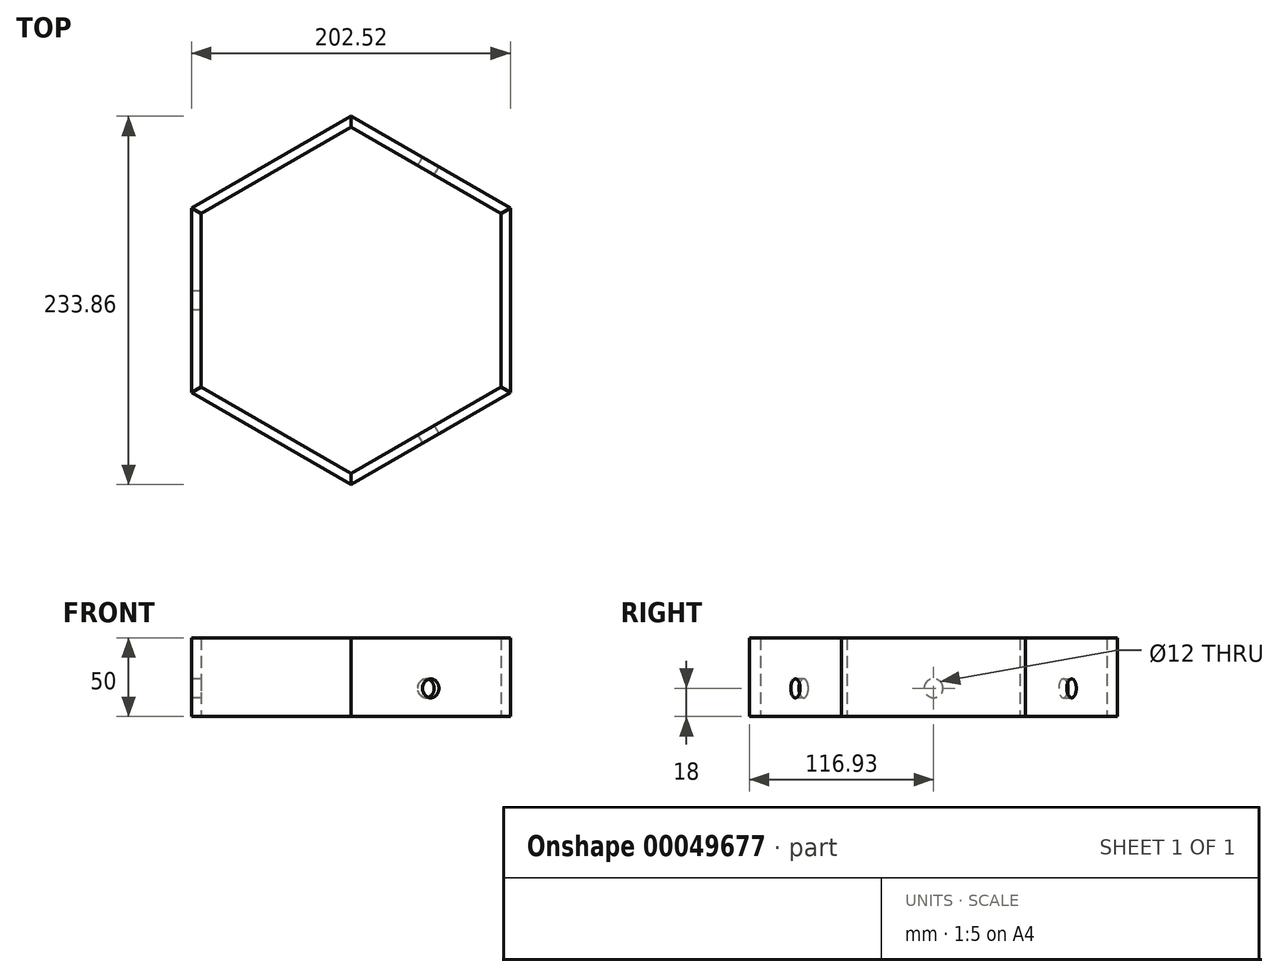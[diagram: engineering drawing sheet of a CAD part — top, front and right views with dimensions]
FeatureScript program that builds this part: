
annotation { "Feature Type Name" : "Feature", "Feature Type Description" : "" }
export const myFeature = defineFeature(function(context is Context, id is Id, definition is map)
    precondition{}
    {
        {
            var Q0;
            Q0=qCreatedBy(makeId("Top.planeOp"),FACE);
            var sketch = newSketch(context, id + "F0", { "sketchPlane" : qUnion([Q0])});
            skCircle(sketch, "E0.cCircle", {"center": v(0, 0) * mm, "radius": 101.26 * mm, "construction": true});
            skLineSegment(sketch, "E0.0", {"start": v(101.26, -58.46) * mm, "end": v(0, -116.93) * mm});
            skLineSegment(sketch, "E0.1", {"start": v(0, -116.93) * mm, "end": v(-101.26, -58.46) * mm});
            skLineSegment(sketch, "E0.2", {"start": v(-101.26, -58.46) * mm, "end": v(-101.26, 58.46) * mm});
            skLineSegment(sketch, "E0.3", {"start": v(-101.26, 58.46) * mm, "end": v(0, 116.93) * mm});
            skLineSegment(sketch, "E0.4", {"start": v(0, 116.93) * mm, "end": v(101.26, 58.46) * mm});
            skLineSegment(sketch, "E0.5", {"start": v(101.26, 58.46) * mm, "end": v(101.26, -58.46) * mm});
            skPoint(sketch, "E0.0.midPoint", {"position": v(50.63, -87.7) * mm});
            skLineSegment(sketch, "E1", {"start": v(0, 116.93) * mm, "end": v(0, -116.93) * mm, "construction": true});
            skLineSegment(sketch, "E2.0", {"start": v(-95.26, -55) * mm, "end": v(-95.26, 55) * mm});
            skLineSegment(sketch, "E2.1", {"start": v(0, 110) * mm, "end": v(95.26, 55) * mm});
            skLineSegment(sketch, "E2.2", {"start": v(95.26, 55) * mm, "end": v(95.26, -55) * mm});
            skLineSegment(sketch, "E2.3", {"start": v(-95.26, 55) * mm, "end": v(0, 110) * mm});
            skLineSegment(sketch, "E2.4", {"start": v(95.26, -55) * mm, "end": v(0, -110) * mm});
            skLineSegment(sketch, "E2.5", {"start": v(0, -110) * mm, "end": v(-95.26, -55) * mm});
            skLineSegment(sketch, "E3", {"start": v(0, 116.93) * mm, "end": v(0, 110) * mm});
            skLineSegment(sketch, "E4", {"start": v(-95.26, 55) * mm, "end": v(-101.26, 58.46) * mm});
            skLineSegment(sketch, "E5", {"start": v(95.26, 55) * mm, "end": v(101.26, 58.46) * mm});
            skLineSegment(sketch, "E6", {"start": v(101.26, -58.46) * mm, "end": v(95.26, -55) * mm});
            skLineSegment(sketch, "E7", {"start": v(-95.26, -55) * mm, "end": v(-101.26, -58.46) * mm});
            skLineSegment(sketch, "E8", {"start": v(0, -110) * mm, "end": v(0, -116.93) * mm});
            skSolve(sketch);
        }
        {
            var Q0;
            Q0=makeQuery(id+"F0.imprint","IMPRINT",FACE,{"disambiguationData":[TD([[makeQuery(id+"F0.imprint","IMPRINT",EDGE,{"derivedFrom":sQuery(id+"F0.wireOp",EDGE,"E0.3")}),-1.0]])]});
            extrude(context, id + "F1", {"entities" : qUnion([Q0]), "depth" : 50 * mm});
        }
        {
            var Q0;
            Q0=makeQuery(id+"F0.imprint","IMPRINT",FACE,{"disambiguationData":[TD([[makeQuery(id+"F0.imprint","IMPRINT",EDGE,{"derivedFrom":sQuery(id+"F0.wireOp",EDGE,"E0.2")}),-1.0]])]});
            extrude(context, id + "F2", {"entities" : qUnion([Q0]), "depth" : 50 * mm});
        }
        {
            var Q0;
            Q0=makeQuery(id+"F0.imprint","IMPRINT",FACE,{"disambiguationData":[TD([[makeQuery(id+"F0.imprint","IMPRINT",EDGE,{"derivedFrom":sQuery(id+"F0.wireOp",EDGE,"E0.1")}),-1.0]])]});
            extrude(context, id + "F3", {"entities" : qUnion([Q0]), "depth" : 50 * mm});
        }
        {
            var Q0;
            Q0=makeQuery(id+"F0.imprint","IMPRINT",FACE,{"disambiguationData":[TD([[makeQuery(id+"F0.imprint","IMPRINT",EDGE,{"derivedFrom":sQuery(id+"F0.wireOp",EDGE,"E0.4")}),-1.0]])]});
            extrude(context, id + "F4", {"entities" : qUnion([Q0]), "depth" : 50 * mm});
        }
        {
            var Q0;
            Q0=makeQuery(id+"F0.imprint","IMPRINT",FACE,{"disambiguationData":[TD([[makeQuery(id+"F0.imprint","IMPRINT",EDGE,{"derivedFrom":sQuery(id+"F0.wireOp",EDGE,"E0.5")}),-1.0]])]});
            extrude(context, id + "F5", {"entities" : qUnion([Q0]), "depth" : 50 * mm});
        }
        {
            var Q0;
            Q0=makeQuery(id+"F0.imprint","IMPRINT",FACE,{"disambiguationData":[TD([[makeQuery(id+"F0.imprint","IMPRINT",EDGE,{"derivedFrom":sQuery(id+"F0.wireOp",EDGE,"E0.0")}),-1.0]])]});
            extrude(context, id + "F6", {"entities" : qUnion([Q0]), "depth" : 50 * mm});
        }
        {
            var Q0;
            Q0=makeQuery(id+"F6.opExtrude","SWEPT_FACE",FACE,{"disambiguationData":[OSD([sQuery(id+"F0.wireOp",EDGE,"E0.0")])]});
            var sketch = newSketch(context, id + "F7", { "sketchPlane" : qUnion([Q0])});
            skLineSegment(sketch, "E9", {"start": v(0, 0) * mm, "end": v(0, 50) * mm, "construction": true});
            skLineSegment(sketch, "E10", {"start": v(-58.46, 18) * mm, "end": v(58.46, 18) * mm, "construction": true});
            skCircle(sketch, "E11", {"center": v(0, 18) * mm, "radius": 6 * mm});
            skSolve(sketch);
        }
        {
            var Q0;
            Q0=makeQuery(id+"F7.imprint","IMPRINT",FACE,{"disambiguationData":[TD([[makeQuery(id+"F7.imprint","IMPRINT",EDGE,{"derivedFrom":sQuery(id+"F7.wireOp",EDGE,"E11")}),1.0]])]});
            extrude(context, id + "F8", {"entities" : qUnion([Q0]), "operationType" : NewBodyOperationType.REMOVE, "oppositeDirection" : true, "depth" : 25 * mm});
        }
        {
            var Q0;
            Q0=makeQuery(id+"F4.opExtrude","SWEPT_FACE",FACE,{"disambiguationData":[OSD([sQuery(id+"F0.wireOp",EDGE,"E0.4")])]});
            var sketch = newSketch(context, id + "F9", { "sketchPlane" : qUnion([Q0])});
            skLineSegment(sketch, "E12", {"start": v(0, 50) * mm, "end": v(0, 0) * mm, "construction": true});
            skLineSegment(sketch, "E13", {"start": v(-58.46, 18) * mm, "end": v(58.46, 18) * mm, "construction": true});
            skCircle(sketch, "E14", {"center": v(0, 18) * mm, "radius": 6 * mm});
            skSolve(sketch);
        }
        {
            var Q0;
            Q0=makeQuery(id+"F2.opExtrude","SWEPT_FACE",FACE,{"disambiguationData":[OSD([sQuery(id+"F0.wireOp",EDGE,"E0.2")])]});
            var sketch = newSketch(context, id + "F10", { "sketchPlane" : qUnion([Q0])});
            skLineSegment(sketch, "E15", {"start": v(-58.46, 18) * mm, "end": v(58.46, 18) * mm, "construction": true});
            skCircle(sketch, "E16", {"center": v(0, 18) * mm, "radius": 6 * mm});
            skSolve(sketch);
        }
        {
            var Q0;
            Q0=makeQuery(id+"F9.imprint","IMPRINT",FACE,{"disambiguationData":[TD([[makeQuery(id+"F9.imprint","IMPRINT",EDGE,{"derivedFrom":sQuery(id+"F9.wireOp",EDGE,"E14")}),1.0]])]});
            extrude(context, id + "F11", {"entities" : qUnion([Q0]), "operationType" : NewBodyOperationType.REMOVE, "oppositeDirection" : true, "depth" : 25 * mm});
        }
        {
            var Q0;
            Q0=makeQuery(id+"F10.imprint","IMPRINT",FACE,{"disambiguationData":[TD([[makeQuery(id+"F10.imprint","IMPRINT",EDGE,{"derivedFrom":sQuery(id+"F10.wireOp",EDGE,"E16")}),1.0]])]});
            extrude(context, id + "F12", {"entities" : qUnion([Q0]), "operationType" : NewBodyOperationType.REMOVE, "oppositeDirection" : true, "depth" : 25 * mm});
        }
    });
